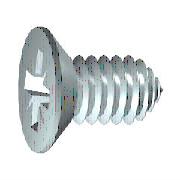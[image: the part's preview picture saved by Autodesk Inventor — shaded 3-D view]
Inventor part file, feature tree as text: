
AUTODESK INVENTOR PART (.ipt)
format: ipt  version: 2020 (Build 240168000, 168)  size: 266,752 bytes
history: native  units: mm (DEFAULTED — no unit token found)
features: extrude x2, plane x1, sketch x1
ambient origin geometry x8: Origin, YZ Plane, XZ Plane, XY Plane, X Axis, Y Axis, Z Axis, Center Point
bodies: Solid1 (feature_tree), Body (feature_tree)
feature tree (4):
  extrude  "Slot"  TaperAngle=45.0deg  [1 undecoded]
  extrude  "Star Cut"  Depth=2.05mm
  plane  "Work Plane2"
  sketch  "Sketch3"  dims[d0=22.0mm d2=45.0deg d3=3.5mm d5=7.3mm d6=4.1mm d7=4.625123mm d8=10.821041mm d9=2.2mm d16=90.0deg d10=45.0deg d11=1.64mm d12=4.1mm d13=0.515mm d14=4.1mm d15=45.0deg d17=0.515mm d18=2.35mm d19=-5.235988mm d20=19.65mm d21=0.0mm d22=1.75mm d23=3.2mm d25=0.0mm d26=2.05mm d66=25.4mm d27=0.872665mm d28=0.206mm d29=2.35mm d71=45.0deg d73=0.0mm d74=0.0mm]
note: 1 required parameter value undecoded (feature->parameter linkage not recoverable at this tier; creation-order binding heuristic only, values carry confidence <= 0.55)
